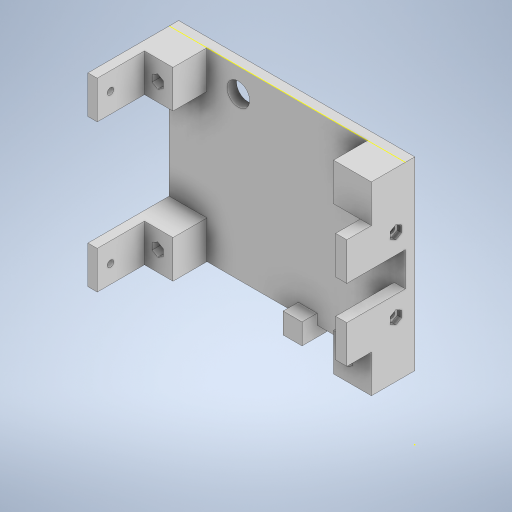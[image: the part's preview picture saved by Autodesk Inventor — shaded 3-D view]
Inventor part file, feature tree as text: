
AUTODESK INVENTOR PART (.ipt)
format: ipt  version: 2024.3 (Build 283343000, 343)  size: 1,389,056 bytes
history: native  units: mm
features: sketch x15, extrude x13, other x7
ambient origin geometry x8: Origin, YZ Plane, XZ Plane, XY Plane, X Axis, Y Axis, Z Axis, Center Point
bodies: Body1 (feature_tree)
feature tree (35):
  other  "Sólido1"
  extrude  "Extrusión1"  Depth=125.0mm
  sketch  "Boceto2"  dims[d2=5.0mm d3=0.0mm d58=86.995mm]
  extrude  "Extrusión2"  Depth=5.0mm
  extrude  "Extrusión3"  Depth=114.174107mm
  extrude  "Extrusión4"  Depth=5.5mm
  extrude  "Extrusión5"  Depth=20.0mm
  extrude  "Extrusión6"  Depth=20.0mm
  extrude  "Extrusión7"  Depth=20.0mm
  sketch  "Boceto9"  dims[d93=20.0mm d95=18.0mm d96=0.0mm]
  extrude  "Extrusión8"  Depth=20.0mm
  extrude  "Extrusión9"  Depth=18.0mm TaperAngle=0.0deg
  extrude  "Extrusión10"  Depth=5.5mm
  extrude  "Extrusión11"  Depth=4.912893mm
  extrude  "Extrusión15"  Depth=25.0mm TaperAngle=0.0deg
  extrude  "Extrusión16"  Depth=5.913mm
  sketch  "Boceto1"  dims[d0=98.0mm d1=125.0mm]
  sketch  "Boceto3"  dims[d62=114.174107mm d67=5.9mm]
  other  "Imagen3"
  sketch  "Boceto4"  dims[d68=4.925893mm d70=5.5mm]
  other  "Imagen4"
  sketch  "Boceto5"  dims[d71=5.505mm d86=20.0mm]
  sketch  "Boceto6"  dims[d87=20.0mm d88=20.0mm]
  other  "Imagen5"
  sketch  "Boceto7"  dims[d89=20.0mm d90=20.0mm]
  sketch  "Boceto8"  dims[d91=20.0mm d92=20.0mm]
  sketch  "Boceto10"  dims[d105=5.5mm d106=5.505mm]
  sketch  "Boceto11"  dims[d108=5.913mm d109=4.912893mm]
  sketch  "Boceto12"  dims[d111=20.0mm d113=25.0mm d114=0.0mm]
  sketch  "Boceto13"  dims[d120=20.0mm d121=5.913mm]
  other  "Imagen6"
  sketch  "Boceto17"  dims[d122=20.0mm]
  sketch  "Boceto18"  dims[d123=31.0mm d124=0.0mm d130=5.913mm d131=5.913mm d132=5.5mm d133=6.267032mm d135=10.0mm d136=46.7mm d137=68.3mm d139=8.0mm d140=0.0mm d141=5.5mm d142=0.0mm d149=3.5mm d151=7.0mm d153=7.0mm d156=3.5mm d157=7.0mm d158=7.0mm d159=2.3mm d160=0.0mm d161=3.5mm d162=3.5mm d163=3.5mm d164=3.5mm d165=3.5mm d166=3.5mm d167=3.5mm d168=3.5mm d169=3.5mm d170=3.5mm d171=3.5mm d172=5.0mm d173=0.0mm d174=7.0mm d175=3.5mm d176=7.0mm d177=3.5mm d178=7.0mm d179=7.0mm d180=2.3mm d181=0.0mm d182=3.5mm d184=3.5mm d187=3.5mm d188=3.5mm d189=3.5mm d190=3.5mm d191=3.5mm d192=3.5mm d193=5.0mm d194=0.0mm d195=3.5mm d196=6.0mm d197=4.0mm d198=6.0mm d199=4.0mm d200=6.0mm d201=4.0mm d202=3.5mm d203=3.5mm d204=6.0mm d205=0.0mm d236=4.0mm d238=3.5mm d239=3.5mm d240=4.0mm d241=3.5mm d243=3.5mm d244=4.0mm d245=3.5mm d246=3.5mm d247=3.5mm d248=3.5mm d249=3.5mm d250=15.0mm d251=0.0mm d283=12.0mm d299=9.588085mm d301=6.5mm d303=7.0mm d305=5.754598mm d307=6.441012mm d308=10.0mm d309=0.0mm d115=0.5mm d116=0.872665mm]
  other  "Imagen9"
  other  "Imagen10"
